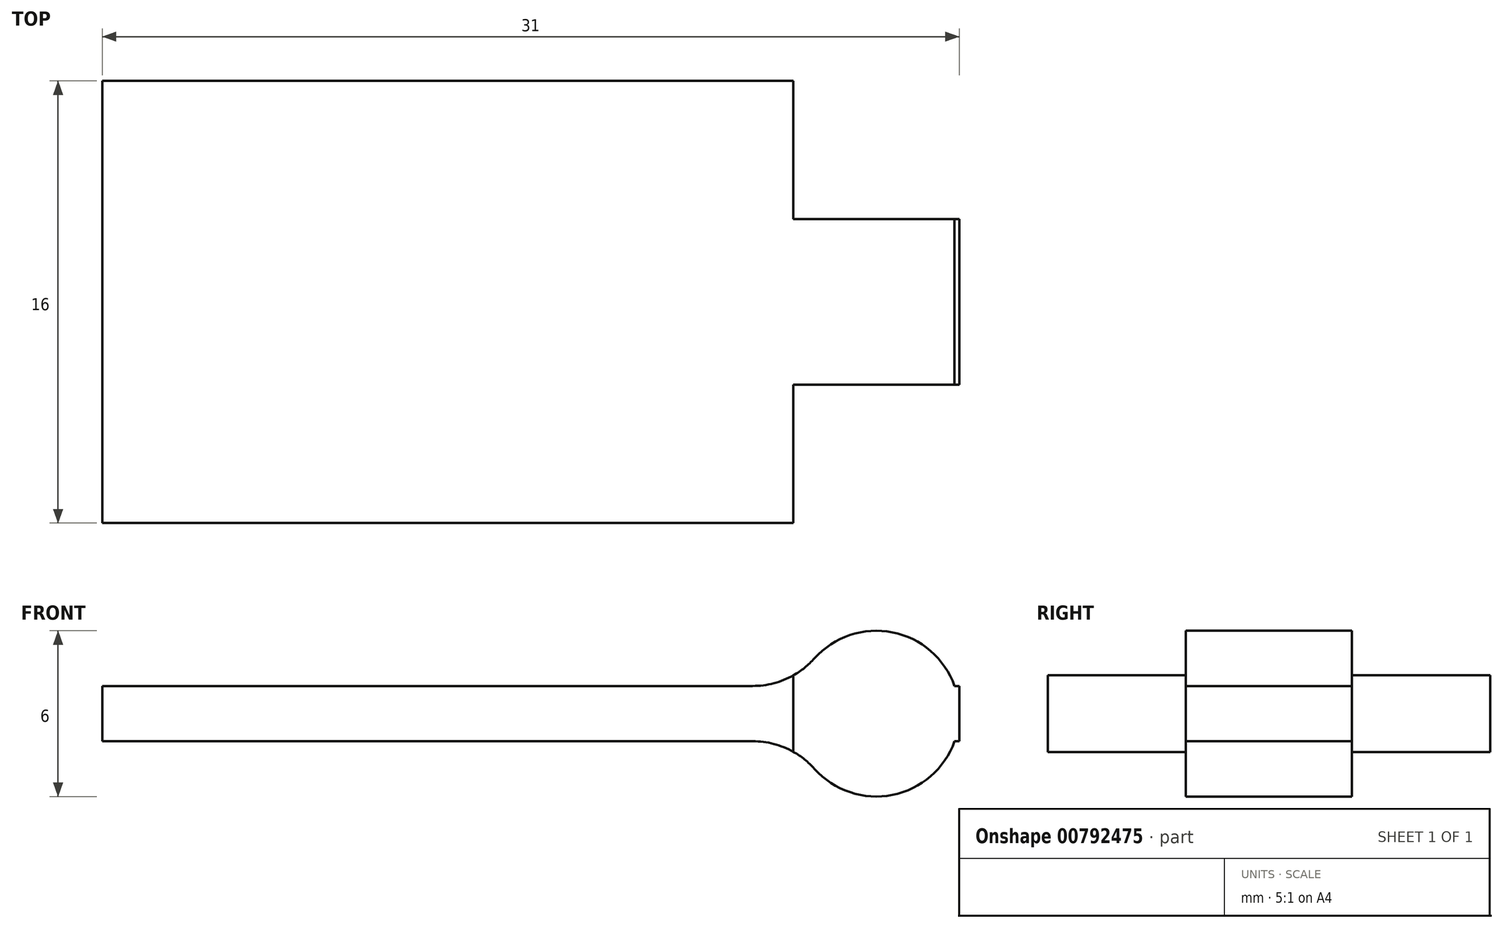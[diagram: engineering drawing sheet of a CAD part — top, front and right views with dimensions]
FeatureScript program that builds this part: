
annotation { "Feature Type Name" : "Feature", "Feature Type Description" : "" }
export const myFeature = defineFeature(function(context is Context, id is Id, definition is map)
    precondition{}
    {
        {
            var Q0;
            Q0=qCreatedBy(makeId("Top.planeOp"),FACE);
            var sketch = newSketch(context, id + "F0", { "sketchPlane" : qUnion([Q0])});
            skLineSegment(sketch, "E0", {"start": v(-28, 0) * mm, "end": v(0, 0) * mm});
            skLineSegment(sketch, "E1.MirrorCS", {"start": v(28, 0) * mm, "end": v(0, 0) * mm});
            skLineSegment(sketch, "E2", {"start": v(-28, 0) * mm, "end": v(-28, 16) * mm});
            skLineSegment(sketch, "E3", {"start": v(-28, 16) * mm, "end": v(0, 16) * mm});
            skLineSegment(sketch, "E4.MirrorCS", {"start": v(28, 0) * mm, "end": v(28, 16) * mm});
            skLineSegment(sketch, "E5.MirrorCS", {"start": v(28, 16) * mm, "end": v(0, 16) * mm});
            skLineSegment(sketch, "E6", {"start": v(3, 11) * mm, "end": v(3, 5) * mm});
            skLineSegment(sketch, "E7.MirrorCS", {"start": v(-3, 16) * mm, "end": v(-3, 11) * mm});
            skLineSegment(sketch, "E8", {"start": v(-3, 11) * mm, "end": v(3, 11) * mm});
            skLineSegment(sketch, "E9", {"start": v(3, 5) * mm, "end": v(-3, 5) * mm});
            skLineSegment(sketch, "E10.trimOffspring", {"start": v(-3, 5) * mm, "end": v(-3, 0) * mm});
            skPoint(sketch, "E11.orphan", {"position": v(3, 16) * mm});
            skPoint(sketch, "E12.orphan", {"position": v(3, 0) * mm});
            skLineSegment(sketch, "E13", {"start": v(3, 11) * mm, "end": v(3, 16) * mm});
            skLineSegment(sketch, "E14", {"start": v(3, 5) * mm, "end": v(3, 0) * mm});
            skLineSegment(sketch, "E15", {"start": v(0, 16) * mm, "end": v(0, 0) * mm});
            skLineSegment(sketch, "E16", {"start": v(0, 11) * mm, "end": v(0, 5) * mm});
            skSolve(sketch);
        }
        {
            var Q0;
            Q0=qCreatedBy(makeId("Front.planeOp"),FACE);
            var sketch = newSketch(context, id + "F1", { "sketchPlane" : qUnion([Q0])});
            skPoint(sketch, "E17", {"position": v(0, 0) * mm});
            skSolve(sketch);
        }
        {
            var Q0;
            {var subQ0=sQuery(id+"F0.wireOp",EDGE,"E6");Q0=makeQuery(id+"F0.imprint","IMPRINT",FACE,{"disambiguationData":[TD([[makeQuery(id+"F0.imprint","IMPRINT",EDGE,{"derivedFrom":subQ0}),-1.0]])]});}
            var Q1;
            Q1=sQuery(id+"F0.wireOp",EDGE,"E15");
            revolve(context, id + "F2", {"surfaceOperationType" : NewSurfaceOperationType.NEW, "entities" : qUnion([Q0]), "axis" : qUnion([Q1]), "revolveType" : RevolveType.FULL});
        }
        {
            var Q0;
            {var subQ1=sQuery(id+"F0.wireOp",EDGE,"E2");Q0=makeQuery(id+"F0.imprint","IMPRINT",FACE,{"disambiguationData":[TD([[makeQuery(id+"F0.imprint","IMPRINT",EDGE,{"derivedFrom":subQ1}),-1.0]])]});}
            var Q1;
            {var subQ0=sQuery(id+"F0.wireOp",EDGE,"E6");Q1=makeQuery(id+"F0.imprint","IMPRINT",FACE,{"disambiguationData":[TD([[makeQuery(id+"F0.imprint","IMPRINT",EDGE,{"derivedFrom":subQ0}),-1.0]])]});}
            extrude(context, id + "F3", {"entities" : qUnion([Q0, Q1]), "endBound" : BoundingType.SYMMETRIC, "depth" : 2 * mm, "offsetDistance" : 25 * mm});
        }
        {
            var Q0;
            Q0=sQuery(id+"F1.wireOp",VERTEX,"E17");
            var Q1;
            Q1=makeQuery(id+"F2.opRevolve","SWEPT_BODY",BODY,{"disambiguationData":[OSD([sQuery(id+"F0.wireOp",EDGE,"E6"),sQuery(id+"F0.wireOp",EDGE,"E8"),sQuery(id+"F0.wireOp",EDGE,"E9"),sQuery(id+"F0.wireOp",EDGE,"E15")])]});
            hole(context, id + "F4", {"style" : HoleStyle.SIMPLE, "endStyle" : HoleEndStyle.THROUGH, "holeDiameter" : 1 * mm, "majorDiameter" : 5 * mm, "isTappedThrough" : true, "tappedDepth" : 12.7 * mm, "tapClearance" : 3, "startFromSketch" : true, "locations" : qUnion([Q0]), "scope" : qUnion([Q1])});
        }
        {
            var Q0;
            Q0=makeQuery(id+"F2.opRevolve","SWEPT_BODY",BODY,{"disambiguationData":[OSD([sQuery(id+"F0.wireOp",EDGE,"E6"),sQuery(id+"F0.wireOp",EDGE,"E8"),sQuery(id+"F0.wireOp",EDGE,"E9"),sQuery(id+"F0.wireOp",EDGE,"E15")])]});
            var Q1;
            Q1=makeQuery(id+"F3.opExtrude","SWEPT_BODY",BODY,{"disambiguationData":[OSD([sQuery(id+"F0.wireOp",EDGE,"E0"),sQuery(id+"F0.wireOp",EDGE,"E2"),sQuery(id+"F0.wireOp",EDGE,"E3"),sQuery(id+"F0.wireOp",EDGE,"E6"),sQuery(id+"F0.wireOp",EDGE,"E7.MirrorCS"),sQuery(id+"F0.wireOp",EDGE,"E8"),sQuery(id+"F0.wireOp",EDGE,"E9"),sQuery(id+"F0.wireOp",EDGE,"E10.trimOffspring")])]});
            booleanBodies(context, id + "F5", {"operationType" : BooleanOperationType.UNION, "tools" : qUnion([Q0, Q1])});
        }
        {
            var Q0;
            {var subQ0=sQuery(id+"F0.wireOp",EDGE,"E6");Q0=makeQuery(id+"F5.opBoolean","INTERSECT",EDGE,{"disambiguationData":[OD(0.0)],"derivedFrom":[makeQuery(id+"F2.opRevolve","SWEPT_FACE",FACE,{"disambiguationData":[OSD([subQ0])]}),makeQuery(id+"F3.opExtrude","CAP_FACE",FACE,{"disambiguationData":[OSD([sQuery(id+"F0.wireOp",EDGE,"E0"),sQuery(id+"F0.wireOp",EDGE,"E2"),sQuery(id+"F0.wireOp",EDGE,"E3"),subQ0,sQuery(id+"F0.wireOp",EDGE,"E7.MirrorCS"),sQuery(id+"F0.wireOp",EDGE,"E8"),sQuery(id+"F0.wireOp",EDGE,"E9"),sQuery(id+"F0.wireOp",EDGE,"E10.trimOffspring")])],"isStart":false})]});}
            var Q1;
            {var subQ0=sQuery(id+"F0.wireOp",EDGE,"E6");Q1=makeQuery(id+"F5.opBoolean","INTERSECT",EDGE,{"disambiguationData":[OD(0.0)],"derivedFrom":[makeQuery(id+"F2.opRevolve","SWEPT_FACE",FACE,{"disambiguationData":[OSD([subQ0])]}),makeQuery(id+"F3.opExtrude","CAP_FACE",FACE,{"disambiguationData":[OSD([sQuery(id+"F0.wireOp",EDGE,"E0"),sQuery(id+"F0.wireOp",EDGE,"E2"),sQuery(id+"F0.wireOp",EDGE,"E3"),subQ0,sQuery(id+"F0.wireOp",EDGE,"E7.MirrorCS"),sQuery(id+"F0.wireOp",EDGE,"E8"),sQuery(id+"F0.wireOp",EDGE,"E9"),sQuery(id+"F0.wireOp",EDGE,"E10.trimOffspring")])],"isStart":true})]});}
            fillet(context, id + "F6", {"entities" : qUnion([Q0, Q1]), "radius" : 3 * mm, "tangentPropagation" : true, "allowEdgeOverflow" : false});
        }
    });
